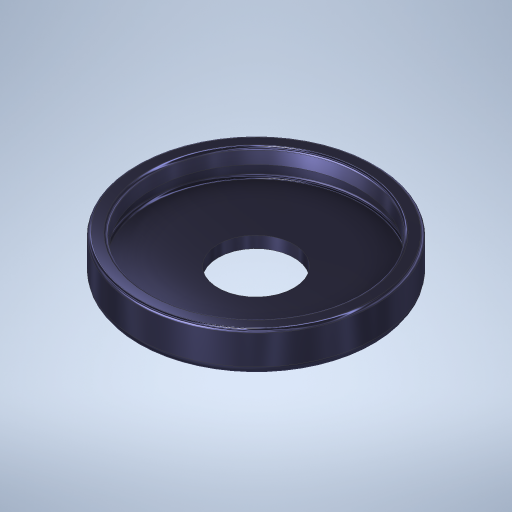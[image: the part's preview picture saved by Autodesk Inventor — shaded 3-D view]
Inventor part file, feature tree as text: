
AUTODESK INVENTOR PART (.ipt)
format: ipt  version: 2023.1 (Build 271208000, 208)  size: 331,264 bytes
history: native  units: in
note: dims shown in document units (in); Inventor stores cm internally (conversion verified against a paired STEP export)
features: fillet x2, revolve x1, sketch x1
ambient origin geometry x8: Origin, YZ Plane, XZ Plane, XY Plane, X Axis, Y Axis, Z Axis, Center Point
bodies: Solid1 (feature_tree)
feature tree (4):
  revolve  "Revolution1"  [1 undecoded]
  fillet  "Fillet1"  Radius=0.07in
  fillet  "Fillet2"  Radius=0.025in
  sketch  "Sketch1"  dims[d0=0.13in d1=0.41in d2=0.07in d3=0.025in d4=0.3558in d5=0.375in d6=0.02in d7=0.025in d8=90.0deg d9=0.015in d10=0.005in]
note: 1 required parameter value undecoded (feature->parameter linkage not recoverable at this tier; creation-order binding heuristic only, values carry confidence <= 0.55)
